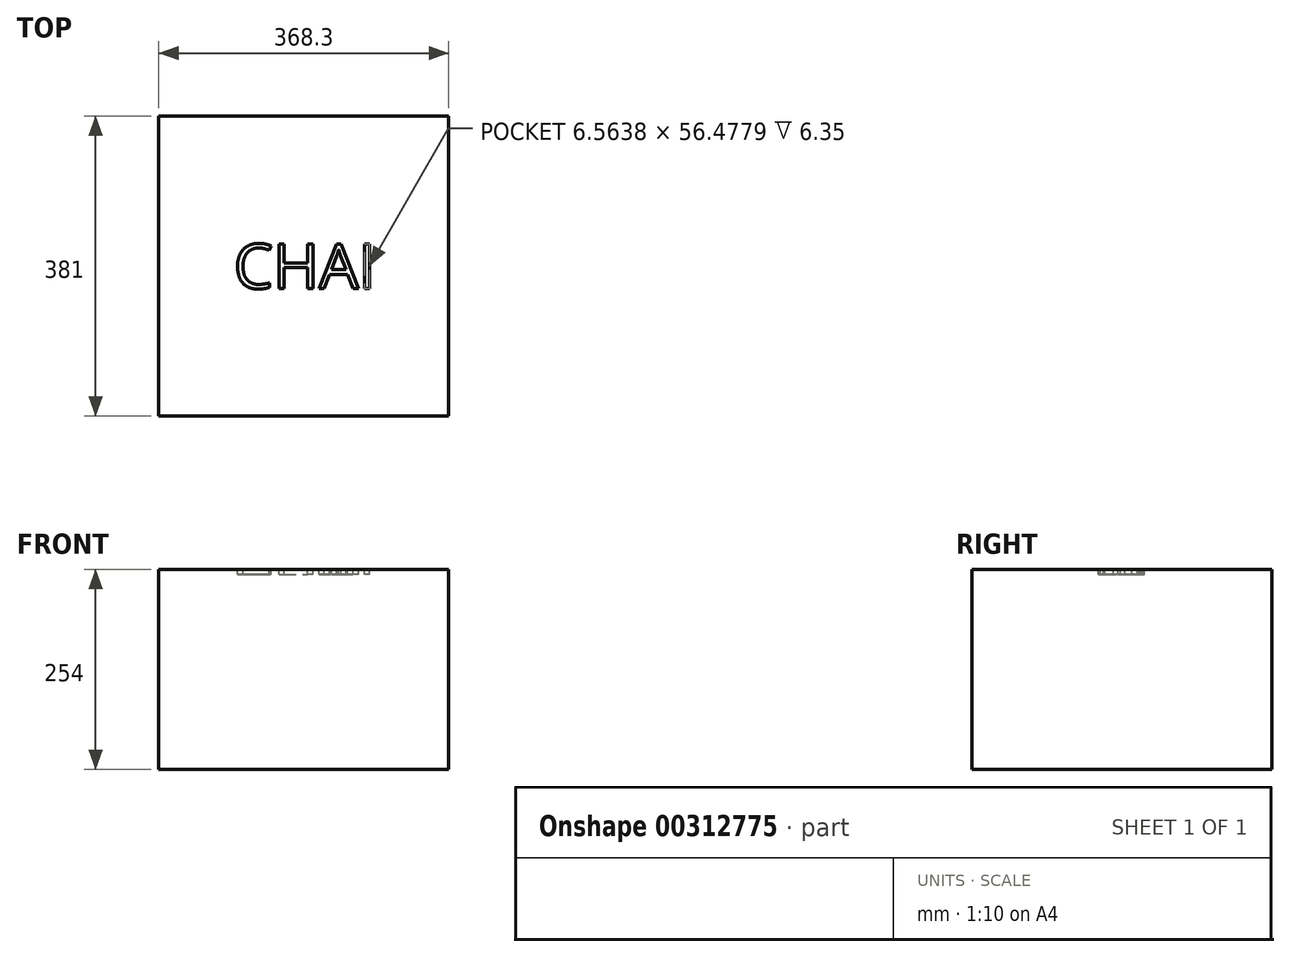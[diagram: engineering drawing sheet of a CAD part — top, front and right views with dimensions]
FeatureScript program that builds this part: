
annotation { "Feature Type Name" : "Feature", "Feature Type Description" : "" }
export const myFeature = defineFeature(function(context is Context, id is Id, definition is map)
    precondition{}
    {
        {
            var Q0;
            Q0=qCreatedBy(makeId("Top.planeOp"),FACE);
            var sketch = newSketch(context, id + "F0", { "sketchPlane" : qUnion([Q0])});
            skLineSegment(sketch, "E0.bottom", {"start": v(0, 0) * mm, "end": v(368.3, 0) * mm});
            skLineSegment(sketch, "E0.top", {"start": v(0, 381) * mm, "end": v(368.3, 381) * mm});
            skLineSegment(sketch, "E0.left", {"start": v(0, 0) * mm, "end": v(0, 381) * mm});
            skLineSegment(sketch, "E0.right", {"start": v(368.3, 0) * mm, "end": v(368.3, 381) * mm});
            skSolve(sketch);
        }
        {
            var Q0;
            Q0=makeQuery(id+"F0.imprint","IMPRINT",FACE,{"disambiguationData":[TD([[makeQuery(id+"F0.imprint","IMPRINT",EDGE,{"derivedFrom":sQuery(id+"F0.wireOp",EDGE,"E0.bottom")}),1.0]])]});
            extrude(context, id + "F1", {"entities" : qUnion([Q0]), "depth" : 254 * mm});
        }
        {
            var Q0;
            Q0=makeQuery(id+"F1.opExtrude","CAP_FACE",FACE,{"disambiguationData":[OSD([sQuery(id+"F0.wireOp",EDGE,"E0.bottom"),sQuery(id+"F0.wireOp",EDGE,"E0.top"),sQuery(id+"F0.wireOp",EDGE,"E0.left"),sQuery(id+"F0.wireOp",EDGE,"E0.right")])],"isStart":false});
            var sketch = newSketch(context, id + "F2", { "sketchPlane" : qUnion([Q0])});
            skText(sketch, "E1", { "text": "CHAI", "fontName": "OpenSans-Regular.ttf"});
            skLineSegment(sketch, "E2", {"start": v(0, 190.5) * mm, "end": v(95.25, 190.5) * mm, "construction": true});
            skLineSegment(sketch, "E3", {"start": v(184.15, 381) * mm, "end": v(184.15, 218.98) * mm, "construction": true});
            const initialGuessF2  = {"E1": [0.09525, 0.16202, 1, 0, 0.05696]};
            skSetInitialGuess(sketch, initialGuessF2);
            skSolve(sketch);
        }
        {
            var Q0;
            Q0 = qSketchRegion(id + "F2", true);
            extrude(context, id + "F3", {"entities" : qUnion([Q0]), "operationType" : NewBodyOperationType.REMOVE, "oppositeDirection" : true, "depth" : 6.35 * mm});
        }
    });
